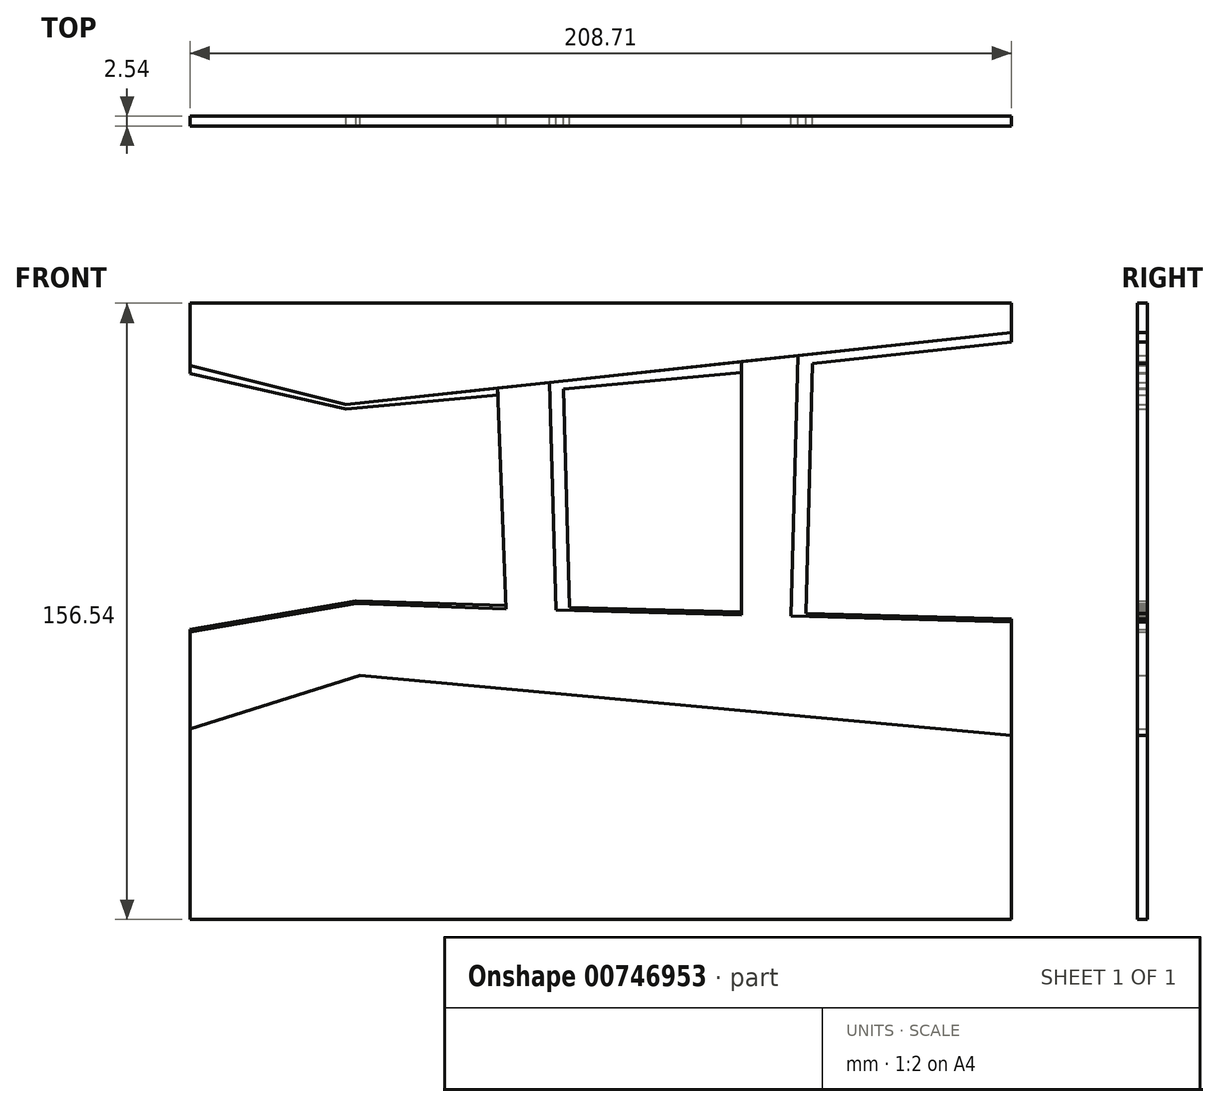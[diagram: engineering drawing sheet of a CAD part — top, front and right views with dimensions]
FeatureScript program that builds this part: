
annotation { "Feature Type Name" : "Feature", "Feature Type Description" : "" }
export const myFeature = defineFeature(function(context is Context, id is Id, definition is map)
    precondition{}
    {
        {
            var Q0;
            Q0=qCreatedBy(makeId("Front.planeOp"),FACE);
            var sketch = newSketch(context, id + "F0", { "sketchPlane" : qUnion([Q0])});
            skSolve(sketch);
        }
        {
            var Q0;
            Q0=qCreatedBy(makeId("Front.planeOp"),FACE);
            var sketch = newSketch(context, id + "F1", { "sketchPlane" : qUnion([Q0])});
            skPoint(sketch, "E0.0", {"position": v(-103.9, 77.23) * mm});
            skPoint(sketch, "E1.0", {"position": v(-103.9, -79.3) * mm});
            skPoint(sketch, "E2.0", {"position": v(104.8, -79.3) * mm});
            skPoint(sketch, "E3.0", {"position": v(104.8, 77.23) * mm});
            skLineSegment(sketch, "E4", {"start": v(-103.9, 77.23) * mm, "end": v(104.8, 77.23) * mm});
            skLineSegment(sketch, "E5", {"start": v(104.8, 77.23) * mm, "end": v(104.8, -79.3) * mm});
            skLineSegment(sketch, "E6", {"start": v(104.8, -79.3) * mm, "end": v(-103.9, -79.3) * mm});
            skLineSegment(sketch, "E7", {"start": v(-103.9, 77.23) * mm, "end": v(-103.9, -79.3) * mm});
            skLineSegment(sketch, "E8", {"start": v(-64.24, 51.55) * mm, "end": v(-103.9, 61.44) * mm});
            skLineSegment(sketch, "E9", {"start": v(-10.92, -0.71) * mm, "end": v(36.2, -1.95) * mm});
            skLineSegment(sketch, "E10", {"start": v(48.81, -2.28) * mm, "end": v(104.8, -3.76) * mm});
            skLineSegment(sketch, "E11", {"start": v(-12.5, 57.13) * mm, "end": v(-10.92, -0.71) * mm});
            skLineSegment(sketch, "E12", {"start": v(-25.74, 55.7) * mm, "end": v(-23.62, -0.38) * mm});
            skLineSegment(sketch, "E13", {"start": v(36.2, 62.4) * mm, "end": v(36.2, -1.95) * mm});
            skLineSegment(sketch, "E14", {"start": v(50.55, 63.94) * mm, "end": v(48.81, -2.28) * mm});
            skLineSegment(sketch, "E15.trimOffspring", {"start": v(36.2, 62.4) * mm, "end": v(-12.5, 57.13) * mm});
            skLineSegment(sketch, "E16.trimOffspring", {"start": v(-25.74, 55.7) * mm, "end": v(-64.24, 51.55) * mm});
            skLineSegment(sketch, "E17", {"start": v(-25.74, 55.7) * mm, "end": v(-12.5, 57.13) * mm});
            skLineSegment(sketch, "E18", {"start": v(-7.48, 0) * mm, "end": v(-9, 55.47) * mm});
            skLineSegment(sketch, "E19", {"start": v(-9, 55.47) * mm, "end": v(36.2, 59.63) * mm});
            skLineSegment(sketch, "E20", {"start": v(-7.48, 0) * mm, "end": v(36.2, -1.15) * mm});
            skLineSegment(sketch, "E21", {"start": v(50.55, 63.94) * mm, "end": v(104.8, 69.8) * mm});
            skLineSegment(sketch, "E22", {"start": v(54.27, 61.9) * mm, "end": v(52.6, -1.56) * mm});
            skLineSegment(sketch, "E23", {"start": v(54.27, 61.9) * mm, "end": v(104.8, 67.37) * mm});
            skLineSegment(sketch, "E24", {"start": v(52.6, -1.56) * mm, "end": v(104.8, -2.93) * mm});
            skLineSegment(sketch, "E25", {"start": v(36.2, 62.4) * mm, "end": v(50.55, 63.94) * mm});
            skLineSegment(sketch, "E26.trimOffspring", {"start": v(-25.68, 53.93) * mm, "end": v(-64.24, 50.38) * mm});
            skLineSegment(sketch, "E27", {"start": v(-64.24, 50.38) * mm, "end": v(-103.9, 59.33) * mm});
            skLineSegment(sketch, "E28", {"start": v(-10.92, -0.71) * mm, "end": v(-7.48, 0) * mm});
            skLineSegment(sketch, "E29", {"start": v(-12.5, 57.13) * mm, "end": v(-9, 55.47) * mm});
            skLineSegment(sketch, "E30", {"start": v(48.81, -2.28) * mm, "end": v(52.6, -1.56) * mm});
            skLineSegment(sketch, "E31", {"start": v(50.55, 63.94) * mm, "end": v(54.27, 61.9) * mm});
            skLineSegment(sketch, "E32", {"start": v(-64.24, 50.38) * mm, "end": v(-61.67, 0.96) * mm});
            skLineSegment(sketch, "E33", {"start": v(-61.67, 0.96) * mm, "end": v(-23.62, -0.38) * mm});
            skLineSegment(sketch, "E34", {"start": v(-61.67, 0.96) * mm, "end": v(-103.9, -6.3) * mm});
            skLineSegment(sketch, "E35", {"start": v(-61.7, 1.56) * mm, "end": v(-103.9, -5.7) * mm});
            skLineSegment(sketch, "E36", {"start": v(-61.67, 0.96) * mm, "end": v(-60.72, -17.37) * mm});
            skLineSegment(sketch, "E37", {"start": v(-60.72, -17.37) * mm, "end": v(104.8, -32.62) * mm});
            skLineSegment(sketch, "E38", {"start": v(-60.72, -17.37) * mm, "end": v(-103.9, -30.96) * mm});
            skLineSegment(sketch, "E39.trimOffspring", {"start": v(-23.65, 0.46) * mm, "end": v(-61.7, 1.56) * mm});
            skLineSegment(sketch, "E40", {"start": v(-64.24, 50.38) * mm, "end": v(-64.24, 51.55) * mm});
            skSolve(sketch);
        }
        {
            var Q0;
            {var subQ2=sQuery(id+"F1.wireOp",EDGE,"E6");Q0=makeQuery(id+"F1.imprint","IMPRINT",FACE,{"disambiguationData":[TD([[makeQuery(id+"F1.imprint","IMPRINT",EDGE,{"derivedFrom":subQ2}),-1.0]])]});}
            extrude(context, id + "F2", {"entities" : qUnion([Q0]), "depth" : 2.54 * mm, "offsetDistance" : 25.4 * mm});
        }
        {
            var Q0;
            {var subQ0=sQuery(id+"F1.wireOp",EDGE,"E34");Q0=makeQuery(id+"F1.imprint","IMPRINT",FACE,{"disambiguationData":[TD([[makeQuery(id+"F1.imprint","IMPRINT",EDGE,{"derivedFrom":subQ0}),1.0]])]});}
            var Q1;
            {var subQ1=sQuery(id+"F1.wireOp",EDGE,"E9");Q1=makeQuery(id+"F1.imprint","IMPRINT",FACE,{"disambiguationData":[TD([[makeQuery(id+"F1.imprint","IMPRINT",EDGE,{"derivedFrom":subQ1}),-1.0]])]});}
            extrude(context, id + "F3", {"entities" : qUnion([Q0, Q1]), "depth" : 2.54 * mm, "offsetDistance" : 25.4 * mm});
        }
        {
            var Q0;
            {var subQ0=sQuery(id+"F1.wireOp",EDGE,"E21");Q0=makeQuery(id+"F1.imprint","IMPRINT",FACE,{"disambiguationData":[TD([[makeQuery(id+"F1.imprint","IMPRINT",EDGE,{"derivedFrom":subQ0}),-1.0]])]});}
            var Q1;
            Q1=makeQuery(id+"F1.imprint","IMPRINT",FACE,{"disambiguationData":[TD([[makeQuery(id+"F1.imprint","IMPRINT",EDGE,{"derivedFrom":sQuery(id+"F1.wireOp",EDGE,"E14")}),1.0]])]});
            var Q2;
            {var subQ0=sQuery(id+"F1.wireOp",EDGE,"E10");Q2=makeQuery(id+"F1.imprint","IMPRINT",FACE,{"disambiguationData":[TD([[makeQuery(id+"F1.imprint","IMPRINT",EDGE,{"derivedFrom":subQ0}),1.0]])]});}
            var Q3;
            {var subQ0=sQuery(id+"F1.wireOp",EDGE,"E9");Q3=makeQuery(id+"F1.imprint","IMPRINT",FACE,{"disambiguationData":[TD([[makeQuery(id+"F1.imprint","IMPRINT",EDGE,{"derivedFrom":subQ0}),1.0]])]});}
            var Q4;
            Q4=makeQuery(id+"F1.imprint","IMPRINT",FACE,{"disambiguationData":[TD([[makeQuery(id+"F1.imprint","IMPRINT",EDGE,{"derivedFrom":sQuery(id+"F1.wireOp",EDGE,"E11")}),1.0]])]});
            var Q5;
            {var subQ0=sQuery(id+"F1.wireOp",EDGE,"E15.trimOffspring");Q5=makeQuery(id+"F1.imprint","IMPRINT",FACE,{"disambiguationData":[TD([[makeQuery(id+"F1.imprint","IMPRINT",EDGE,{"derivedFrom":subQ0}),1.0]])]});}
            var Q6;
            {var subQ0=sQuery(id+"F1.wireOp",EDGE,"E16.trimOffspring");Q6=makeQuery(id+"F1.imprint","IMPRINT",FACE,{"disambiguationData":[TD([[makeQuery(id+"F1.imprint","IMPRINT",EDGE,{"derivedFrom":subQ0}),1.0]])]});}
            var Q7;
            {var subQ0=sQuery(id+"F1.wireOp",EDGE,"E8");Q7=makeQuery(id+"F1.imprint","IMPRINT",FACE,{"disambiguationData":[TD([[makeQuery(id+"F1.imprint","IMPRINT",EDGE,{"derivedFrom":subQ0}),1.0]])]});}
            var Q8;
            {var subQ0=sQuery(id+"F1.wireOp",EDGE,"E34");Q8=makeQuery(id+"F1.imprint","IMPRINT",FACE,{"disambiguationData":[TD([[makeQuery(id+"F1.imprint","IMPRINT",EDGE,{"derivedFrom":subQ0}),-1.0]])]});}
            var Q9;
            {var subQ0=sQuery(id+"F1.wireOp",EDGE,"E33");Q9=makeQuery(id+"F1.imprint","IMPRINT",FACE,{"disambiguationData":[TD([[makeQuery(id+"F1.imprint","IMPRINT",EDGE,{"derivedFrom":subQ0}),1.0]])]});}
            extrude(context, id + "F4", {"entities" : qUnion([Q0, Q1, Q2, Q3, Q4, Q5, Q6, Q7, Q8, Q9]), "depth" : 2.54 * mm, "offsetDistance" : 25.4 * mm});
        }
        {
            var Q0;
            {var subQ2=sQuery(id+"F1.wireOp",EDGE,"E4");Q0=makeQuery(id+"F1.imprint","IMPRINT",FACE,{"disambiguationData":[TD([[makeQuery(id+"F1.imprint","IMPRINT",EDGE,{"derivedFrom":subQ2}),-1.0]])]});}
            extrude(context, id + "F5", {"entities" : qUnion([Q0]), "depth" : 2.54 * mm, "offsetDistance" : 25.4 * mm});
        }
    });
